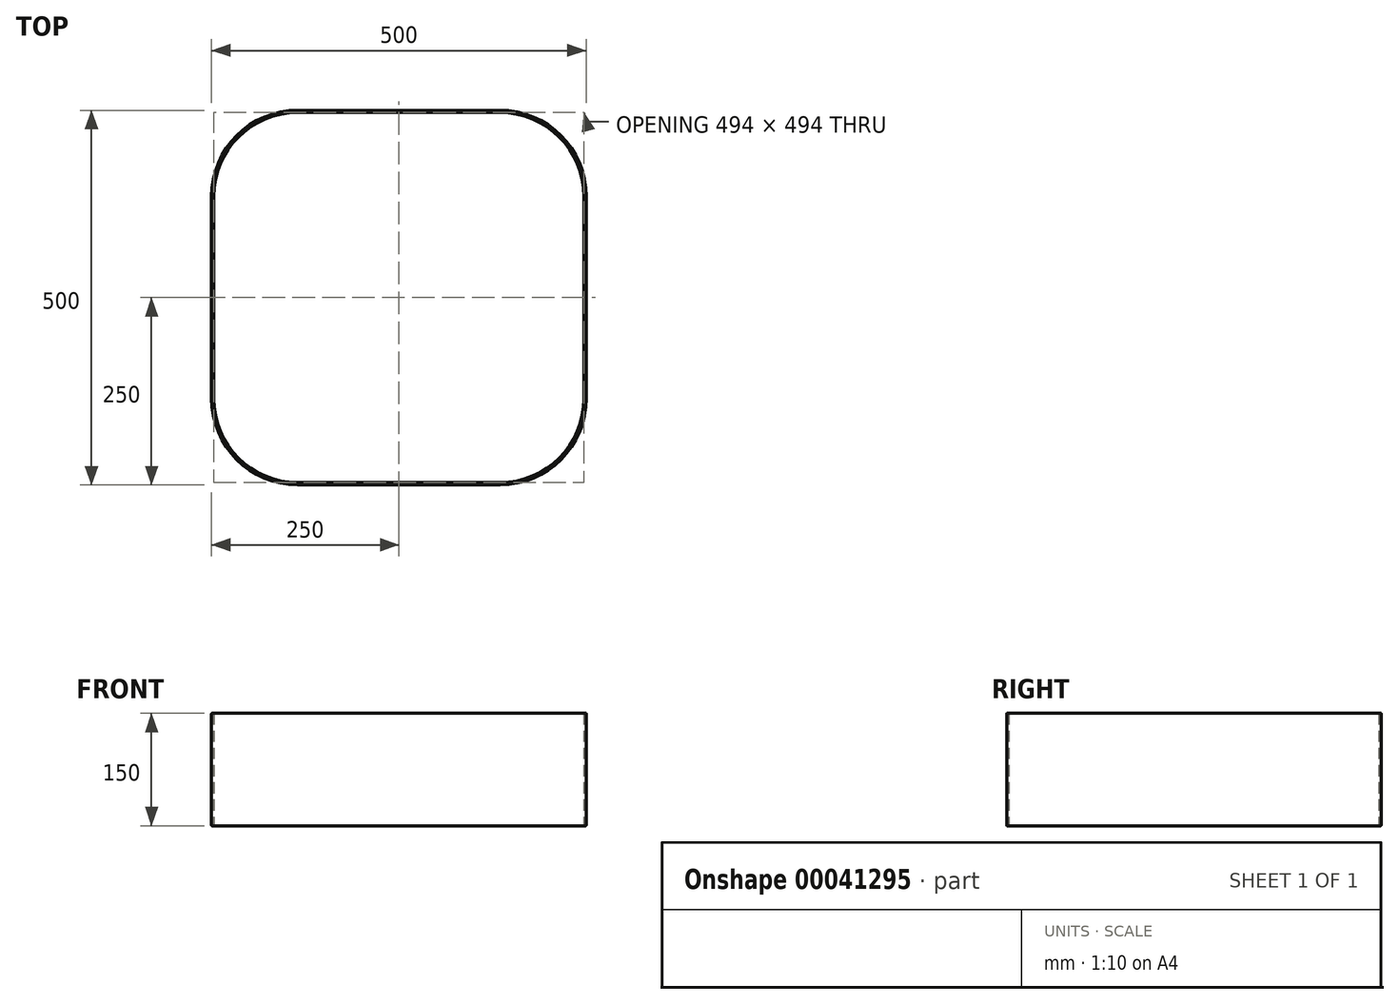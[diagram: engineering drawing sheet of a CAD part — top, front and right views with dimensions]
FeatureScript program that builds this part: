
annotation { "Feature Type Name" : "Feature", "Feature Type Description" : "" }
export const myFeature = defineFeature(function(context is Context, id is Id, definition is map)
    precondition{}
    {
        {
            var Q0;
            Q0=qCreatedBy(makeId("Top.planeOp"),FACE);
            var sketch = newSketch(context, id + "F0", { "sketchPlane" : qUnion([Q0])});
            skLineSegment(sketch, "E0.bottom", {"start": v(-135, 250) * mm, "end": v(135, 250) * mm});
            skLineSegment(sketch, "E0.top", {"start": v(-135, -250) * mm, "end": v(135, -250) * mm});
            skLineSegment(sketch, "E0.left", {"start": v(-250, 135) * mm, "end": v(-250, -135) * mm});
            skLineSegment(sketch, "E0.right", {"start": v(250, 135) * mm, "end": v(250, -135) * mm});
            skPoint(sketch, "E1.visualSharp", {"position": v(-250, 250) * mm});
            skArc(sketch, "E1.filletArc", {"start": v(-135, 250) * mm, "mid": v(-216.32, 216.32) * mm, "end": v(-250, 135) * mm});
            skPoint(sketch, "E2.visualSharp", {"position": v(-250, -250) * mm});
            skArc(sketch, "E2.filletArc", {"start": v(-250, -135) * mm, "mid": v(-216.32, -216.32) * mm, "end": v(-135, -250) * mm});
            skPoint(sketch, "E3.visualSharp", {"position": v(250, -250) * mm});
            skArc(sketch, "E3.filletArc", {"start": v(135, -250) * mm, "mid": v(216.32, -216.32) * mm, "end": v(250, -135) * mm});
            skPoint(sketch, "E4.visualSharp", {"position": v(250, 250) * mm});
            skArc(sketch, "E4.filletArc", {"start": v(250, 135) * mm, "mid": v(216.32, 216.32) * mm, "end": v(135, 250) * mm});
            skLineSegment(sketch, "E5.0", {"start": v(-135, 247) * mm, "end": v(135, 247) * mm});
            skArc(sketch, "E5.1", {"start": v(247, 135) * mm, "mid": v(214.2, 214.2) * mm, "end": v(135, 247) * mm});
            skArc(sketch, "E5.2", {"start": v(-135, 247) * mm, "mid": v(-214.2, 214.2) * mm, "end": v(-247, 135) * mm});
            skLineSegment(sketch, "E5.3", {"start": v(247, 135) * mm, "end": v(247, -135) * mm});
            skLineSegment(sketch, "E5.4", {"start": v(-247, 135) * mm, "end": v(-247, -135) * mm});
            skArc(sketch, "E5.5", {"start": v(-247, -135) * mm, "mid": v(-214.2, -214.2) * mm, "end": v(-135, -247) * mm});
            skLineSegment(sketch, "E5.6", {"start": v(-135, -247) * mm, "end": v(135, -247) * mm});
            skArc(sketch, "E5.7", {"start": v(135, -247) * mm, "mid": v(214.2, -214.2) * mm, "end": v(247, -135) * mm});
            skSolve(sketch);
        }
        {
            var Q0;
            Q0=makeQuery(id+"F0.imprint","IMPRINT",FACE,{"disambiguationData":[TD([[makeQuery(id+"F0.imprint","IMPRINT",EDGE,{"derivedFrom":sQuery(id+"F0.wireOp",EDGE,"E0.bottom")}),-1.0]])]});
            extrude(context, id + "F1", {"entities" : qUnion([Q0]), "depth" : 150 * mm});
        }
        {
            var Q0;
            Q0=makeQuery(id+"F1.opExtrude","CAP_EDGE",EDGE,{"disambiguationData":[OSD([sQuery(id+"F0.wireOp",EDGE,"E0.top")])],"isStart":false});
            var Q1;
            Q1=makeQuery(id+"F1.opExtrude","CAP_EDGE",EDGE,{"disambiguationData":[OSD([sQuery(id+"F0.wireOp",EDGE,"E3.filletArc")])],"isStart":false});
            var Q2;
            Q2=makeQuery(id+"F1.opExtrude","CAP_EDGE",EDGE,{"disambiguationData":[OSD([sQuery(id+"F0.wireOp",EDGE,"E0.right")])],"isStart":false});
            var Q3;
            Q3=makeQuery(id+"F1.opExtrude","CAP_EDGE",EDGE,{"disambiguationData":[OSD([sQuery(id+"F0.wireOp",EDGE,"E4.filletArc")])],"isStart":false});
            var Q4;
            Q4=makeQuery(id+"F1.opExtrude","CAP_EDGE",EDGE,{"disambiguationData":[OSD([sQuery(id+"F0.wireOp",EDGE,"E0.bottom")])],"isStart":false});
            var Q5;
            Q5=makeQuery(id+"F1.opExtrude","CAP_EDGE",EDGE,{"disambiguationData":[OSD([sQuery(id+"F0.wireOp",EDGE,"E1.filletArc")])],"isStart":false});
            var Q6;
            Q6=makeQuery(id+"F1.opExtrude","CAP_EDGE",EDGE,{"disambiguationData":[OSD([sQuery(id+"F0.wireOp",EDGE,"E0.left")])],"isStart":false});
            var Q7;
            Q7=makeQuery(id+"F1.opExtrude","CAP_EDGE",EDGE,{"disambiguationData":[OSD([sQuery(id+"F0.wireOp",EDGE,"E2.filletArc")])],"isStart":false});
            var Q8;
            Q8=makeQuery(id+"F1.opExtrude","CAP_EDGE",EDGE,{"disambiguationData":[OSD([sQuery(id+"F0.wireOp",EDGE,"E0.top")])],"isStart":true});
            var Q9;
            Q9=makeQuery(id+"F1.opExtrude","CAP_EDGE",EDGE,{"disambiguationData":[OSD([sQuery(id+"F0.wireOp",EDGE,"E2.filletArc")])],"isStart":true});
            var Q10;
            Q10=makeQuery(id+"F1.opExtrude","CAP_EDGE",EDGE,{"disambiguationData":[OSD([sQuery(id+"F0.wireOp",EDGE,"E0.left")])],"isStart":true});
            var Q11;
            Q11=makeQuery(id+"F1.opExtrude","CAP_EDGE",EDGE,{"disambiguationData":[OSD([sQuery(id+"F0.wireOp",EDGE,"E1.filletArc")])],"isStart":true});
            var Q12;
            Q12=makeQuery(id+"F1.opExtrude","CAP_EDGE",EDGE,{"disambiguationData":[OSD([sQuery(id+"F0.wireOp",EDGE,"E0.bottom")])],"isStart":true});
            var Q13;
            Q13=makeQuery(id+"F1.opExtrude","CAP_EDGE",EDGE,{"disambiguationData":[OSD([sQuery(id+"F0.wireOp",EDGE,"E4.filletArc")])],"isStart":true});
            var Q14;
            Q14=makeQuery(id+"F1.opExtrude","CAP_EDGE",EDGE,{"disambiguationData":[OSD([sQuery(id+"F0.wireOp",EDGE,"E0.right")])],"isStart":true});
            var Q15;
            Q15=makeQuery(id+"F1.opExtrude","CAP_EDGE",EDGE,{"disambiguationData":[OSD([sQuery(id+"F0.wireOp",EDGE,"E3.filletArc")])],"isStart":true});
            fillet(context, id + "F2", {"entities" : qUnion([Q0, Q1, Q2, Q3, Q4, Q5, Q6, Q7, Q8, Q9, Q10, Q11, Q12, Q13, Q14, Q15]), "radius" : 0.5 * mm, "allowEdgeOverflow" : false});
        }
    });
